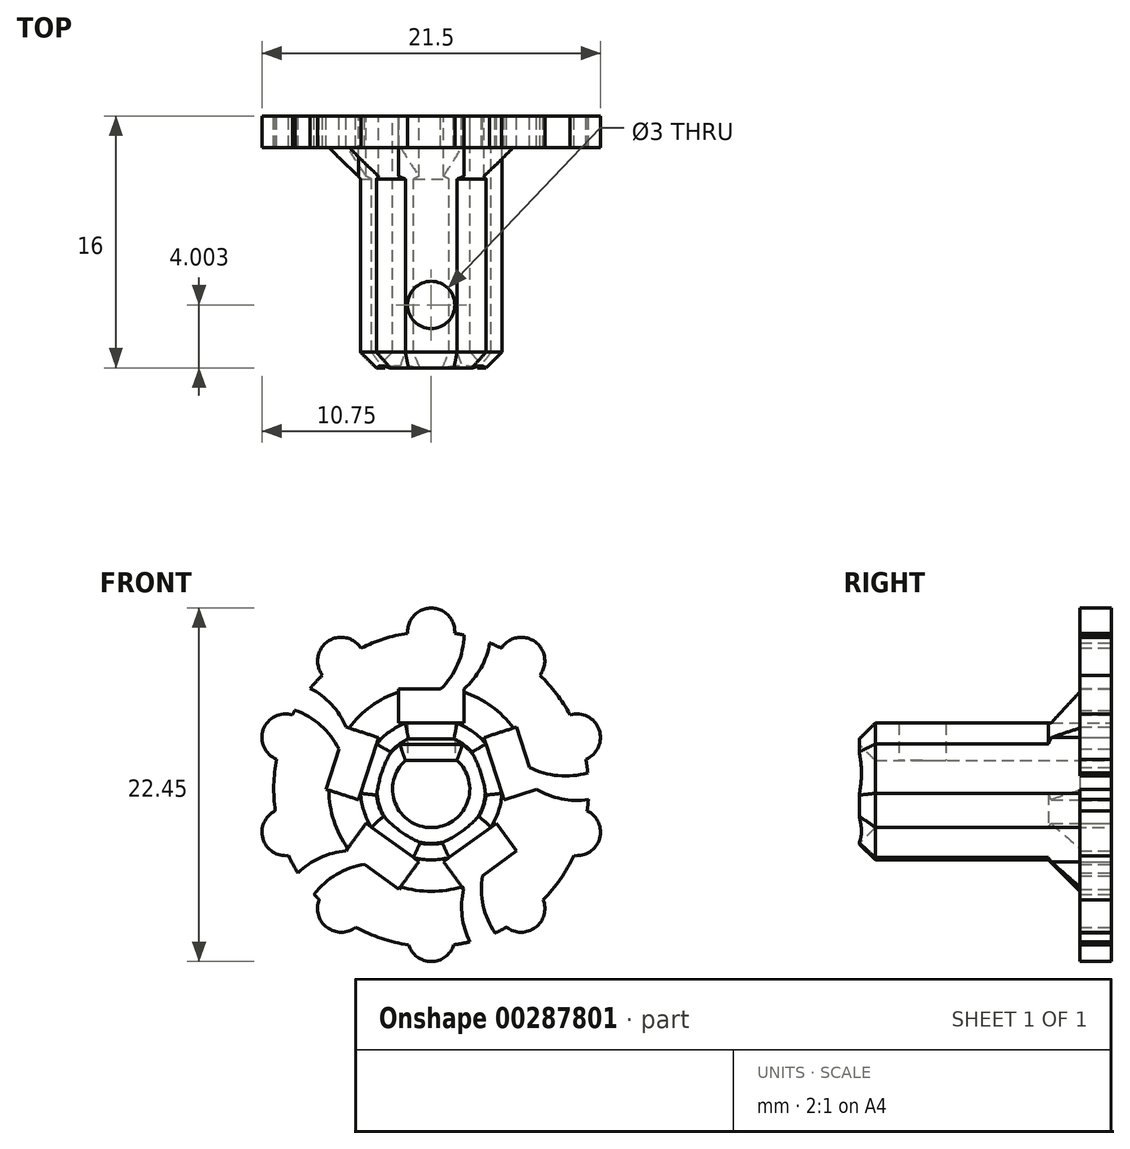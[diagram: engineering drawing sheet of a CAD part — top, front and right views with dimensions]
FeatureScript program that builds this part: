
annotation { "Feature Type Name" : "Feature", "Feature Type Description" : "" }
export const myFeature = defineFeature(function(context is Context, id is Id, definition is map)
    precondition{}
    {
        {
            var Q0;
            Q0=qCreatedBy(makeId("Front.planeOp"),FACE);
            var sketch = newSketch(context, id + "F0", { "sketchPlane" : qUnion([Q0])});
            skCircle(sketch, "E0", {"center": v(0, 0) * mm, "radius": 2.45 * mm});
            skLineSegment(sketch, "E1", {"start": v(-1.64, 1.82) * mm, "end": v(1.64, 1.82) * mm});
            skCircle(sketch, "E2", {"center": v(0, 0) * mm, "radius": 10 * mm});
            skArc(sketch, "E3", {"start": v(1.5, 9.89) * mm, "mid": v(0, 11.5) * mm, "end": v(-1.5, 9.89) * mm});
            skArc(sketch, "E4.1.0", {"start": v(-4.44, 8.93) * mm, "mid": v(-6.6, 9.36) * mm, "end": v(-6.86, 7.17) * mm});
            skArc(sketch, "E4.2.0", {"start": v(-8.68, 4.67) * mm, "mid": v(-10.68, 3.74) * mm, "end": v(-9.6, 1.82) * mm});
            skArc(sketch, "E4.3.0", {"start": v(-9.6, -1.27) * mm, "mid": v(-10.68, -3.2) * mm, "end": v(-8.68, -4.12) * mm});
            skArc(sketch, "E4.4.0", {"start": v(-6.86, -6.62) * mm, "mid": v(-6.6, -8.8) * mm, "end": v(-4.44, -8.38) * mm});
            skArc(sketch, "E4.5.0", {"start": v(-1.5, -9.34) * mm, "mid": v(0, -10.95) * mm, "end": v(1.5, -9.34) * mm});
            skArc(sketch, "E4.6.0", {"start": v(4.44, -8.38) * mm, "mid": v(6.6, -8.8) * mm, "end": v(6.86, -6.62) * mm});
            skArc(sketch, "E4.7.0", {"start": v(8.68, -4.12) * mm, "mid": v(10.68, -3.2) * mm, "end": v(9.6, -1.27) * mm});
            skArc(sketch, "E4.8.0", {"start": v(9.6, 1.82) * mm, "mid": v(10.68, 3.74) * mm, "end": v(8.68, 4.67) * mm});
            skArc(sketch, "E4.9.0", {"start": v(6.86, 7.17) * mm, "mid": v(6.6, 9.36) * mm, "end": v(4.44, 8.93) * mm});
            skPoint(sketch, "E4.center", {"position": v(0, 0.27) * mm});
            skPoint(sketch, "E5.1.0", {"position": v(0.35, -0.11) * mm});
            skLineSegment(sketch, "E6.bottom", {"start": v(2.08, 6.36) * mm, "end": v(-2.07, 6.36) * mm});
            skLineSegment(sketch, "E6.top", {"start": v(2.08, 4.2) * mm, "end": v(-2.07, 4.2) * mm});
            skLineSegment(sketch, "E6.left", {"start": v(2.08, 6.36) * mm, "end": v(2.08, 4.2) * mm});
            skLineSegment(sketch, "E6.right", {"start": v(-2.07, 6.36) * mm, "end": v(-2.07, 4.2) * mm});
            skPoint(sketch, "E6.middle", {"position": v(0, 5.27) * mm});
            skArc(sketch, "E7", {"start": v(0.6, 6.36) * mm, "mid": v(1.68, 7.93) * mm, "end": v(2.1, 9.78) * mm});
            skArc(sketch, "E8", {"start": v(2.08, 6.36) * mm, "mid": v(3.15, 7.68) * mm, "end": v(3.72, 9.28) * mm});
            skLineSegment(sketch, "E9.1.0", {"start": v(-3.34, 3.27) * mm, "end": v(-4.63, -0.68) * mm});
            skArc(sketch, "E9.1.1", {"start": v(-5.86, 2.54) * mm, "mid": v(-7.02, 4.05) * mm, "end": v(-8.65, 5) * mm});
            skLineSegment(sketch, "E9.1.2", {"start": v(-5.4, 3.94) * mm, "end": v(-6.69, 0) * mm});
            skLineSegment(sketch, "E9.1.3", {"start": v(-5.4, 3.94) * mm, "end": v(-3.34, 3.27) * mm});
            skPoint(sketch, "E9.1.4", {"position": v(-5.02, 1.63) * mm});
            skArc(sketch, "E9.1.5", {"start": v(-5.4, 3.94) * mm, "mid": v(-6.33, 5.37) * mm, "end": v(-7.68, 6.4) * mm});
            skLineSegment(sketch, "E9.1.6", {"start": v(-6.69, 0) * mm, "end": v(-4.63, -0.68) * mm});
            skLineSegment(sketch, "E9.2.0", {"start": v(-4.14, -2.17) * mm, "end": v(-0.78, -4.6) * mm});
            skArc(sketch, "E9.2.1", {"start": v(-4.23, -4.79) * mm, "mid": v(-6.02, -5.43) * mm, "end": v(-7.44, -6.68) * mm});
            skLineSegment(sketch, "E9.2.2", {"start": v(-5.42, -3.92) * mm, "end": v(-2.06, -6.36) * mm});
            skLineSegment(sketch, "E9.2.3", {"start": v(-5.42, -3.92) * mm, "end": v(-4.14, -2.17) * mm});
            skPoint(sketch, "E9.2.4", {"position": v(-3.1, -4.27) * mm});
            skArc(sketch, "E9.2.5", {"start": v(-5.42, -3.92) * mm, "mid": v(-7.06, -4.36) * mm, "end": v(-8.46, -5.33) * mm});
            skLineSegment(sketch, "E9.2.6", {"start": v(-2.06, -6.36) * mm, "end": v(-0.78, -4.6) * mm});
            skLineSegment(sketch, "E9.3.0", {"start": v(0.78, -4.6) * mm, "end": v(4.14, -2.17) * mm});
            skArc(sketch, "E9.3.1", {"start": v(3.25, -5.5) * mm, "mid": v(3.3, -7.4) * mm, "end": v(4.06, -9.14) * mm});
            skLineSegment(sketch, "E9.3.2", {"start": v(2.06, -6.36) * mm, "end": v(5.42, -3.92) * mm});
            skLineSegment(sketch, "E9.3.3", {"start": v(2.06, -6.36) * mm, "end": v(0.78, -4.6) * mm});
            skPoint(sketch, "E9.3.4", {"position": v(3.1, -4.27) * mm});
            skArc(sketch, "E9.3.5", {"start": v(2.06, -6.36) * mm, "mid": v(1.97, -8.06) * mm, "end": v(2.45, -9.7) * mm});
            skLineSegment(sketch, "E9.3.6", {"start": v(5.42, -3.92) * mm, "end": v(4.14, -2.17) * mm});
            skLineSegment(sketch, "E9.4.0", {"start": v(4.63, -0.68) * mm, "end": v(3.34, 3.27) * mm});
            skArc(sketch, "E9.4.1", {"start": v(6.23, 1.39) * mm, "mid": v(8.06, 0.85) * mm, "end": v(9.95, 1.03) * mm});
            skLineSegment(sketch, "E9.4.2", {"start": v(6.69, 0) * mm, "end": v(5.4, 3.94) * mm});
            skLineSegment(sketch, "E9.4.3", {"start": v(6.69, 0) * mm, "end": v(4.63, -0.68) * mm});
            skPoint(sketch, "E9.4.4", {"position": v(5.02, 1.63) * mm});
            skArc(sketch, "E9.4.5", {"start": v(6.69, 0) * mm, "mid": v(8.28, -0.62) * mm, "end": v(9.98, -0.67) * mm});
            skLineSegment(sketch, "E9.4.6", {"start": v(5.4, 3.94) * mm, "end": v(3.34, 3.27) * mm});
            skSolve(sketch);
        }
        {
            var Q0;
            Q0=makeQuery(id+"F0.imprint","IMPRINT",FACE,{"disambiguationData":[TD([[makeQuery(id+"F0.imprint","IMPRINT",EDGE,{"derivedFrom":sQuery(id+"F0.wireOp",EDGE,"E2")}),1.0]])]});
            var Q1;
            {var subQ0=sQuery(id+"F0.wireOp",EDGE,"E1");Q1=makeQuery(id+"F0.imprint","IMPRINT",FACE,{"disambiguationData":[TD([[makeQuery(id+"F0.imprint","IMPRINT",EDGE,{"derivedFrom":subQ0}),1.0]])]});}
            var Q2;
            {var subQ0=sQuery(id+"F0.wireOp",EDGE,"E3");Q2=makeQuery(id+"F0.imprint","IMPRINT",FACE,{"disambiguationData":[TD([[makeQuery(id+"F0.imprint","IMPRINT",EDGE,{"derivedFrom":subQ0}),1.0]])]});}
            var Q3;
            {var subQ0=sQuery(id+"F0.wireOp",EDGE,"E4.9.0");Q3=makeQuery(id+"F0.imprint","IMPRINT",FACE,{"disambiguationData":[TD([[makeQuery(id+"F0.imprint","IMPRINT",EDGE,{"derivedFrom":subQ0}),1.0]])]});}
            var Q4;
            {var subQ0=sQuery(id+"F0.wireOp",EDGE,"E4.8.0");Q4=makeQuery(id+"F0.imprint","IMPRINT",FACE,{"disambiguationData":[TD([[makeQuery(id+"F0.imprint","IMPRINT",EDGE,{"derivedFrom":subQ0}),1.0]])]});}
            var Q5;
            {var subQ0=sQuery(id+"F0.wireOp",EDGE,"E4.7.0");Q5=makeQuery(id+"F0.imprint","IMPRINT",FACE,{"disambiguationData":[TD([[makeQuery(id+"F0.imprint","IMPRINT",EDGE,{"derivedFrom":subQ0}),1.0]])]});}
            var Q6;
            {var subQ0=sQuery(id+"F0.wireOp",EDGE,"E4.6.0");Q6=makeQuery(id+"F0.imprint","IMPRINT",FACE,{"disambiguationData":[TD([[makeQuery(id+"F0.imprint","IMPRINT",EDGE,{"derivedFrom":subQ0}),1.0]])]});}
            var Q7;
            {var subQ0=sQuery(id+"F0.wireOp",EDGE,"E4.5.0");Q7=makeQuery(id+"F0.imprint","IMPRINT",FACE,{"disambiguationData":[TD([[makeQuery(id+"F0.imprint","IMPRINT",EDGE,{"derivedFrom":subQ0}),1.0]])]});}
            var Q8;
            {var subQ0=sQuery(id+"F0.wireOp",EDGE,"E4.4.0");Q8=makeQuery(id+"F0.imprint","IMPRINT",FACE,{"disambiguationData":[TD([[makeQuery(id+"F0.imprint","IMPRINT",EDGE,{"derivedFrom":subQ0}),1.0]])]});}
            var Q9;
            {var subQ0=sQuery(id+"F0.wireOp",EDGE,"E4.3.0");Q9=makeQuery(id+"F0.imprint","IMPRINT",FACE,{"disambiguationData":[TD([[makeQuery(id+"F0.imprint","IMPRINT",EDGE,{"derivedFrom":subQ0}),1.0]])]});}
            var Q10;
            {var subQ0=sQuery(id+"F0.wireOp",EDGE,"E4.2.0");Q10=makeQuery(id+"F0.imprint","IMPRINT",FACE,{"disambiguationData":[TD([[makeQuery(id+"F0.imprint","IMPRINT",EDGE,{"derivedFrom":subQ0}),1.0]])]});}
            var Q11;
            {var subQ0=sQuery(id+"F0.wireOp",EDGE,"E4.1.0");Q11=makeQuery(id+"F0.imprint","IMPRINT",FACE,{"disambiguationData":[TD([[makeQuery(id+"F0.imprint","IMPRINT",EDGE,{"derivedFrom":subQ0}),1.0]])]});}
            extrude(context, id + "F1", {"entities" : qUnion([Q0, Q1, Q2, Q3, Q4, Q5, Q6, Q7, Q8, Q9, Q10, Q11]), "depth" : 2 * mm});
        }
        {
            var Q0;
            Q0=makeQuery(id+"F1.opExtrude","CAP_FACE",FACE,{"disambiguationData":[OSD([sQuery(id+"F0.wireOp",EDGE,"E0"),sQuery(id+"F0.wireOp",EDGE,"E1"),sQuery(id+"F0.wireOp",EDGE,"E2")])],"isStart":false});
            var sketch = newSketch(context, id + "F2", { "sketchPlane" : qUnion([Q0])});
            skCircle(sketch, "E10", {"center": v(0, 0) * mm, "radius": 2.45 * mm});
            skCircle(sketch, "E11", {"center": v(0, 0) * mm, "radius": 4.5 * mm});
            skLineSegment(sketch, "E12", {"start": v(-1.64, 1.82) * mm, "end": v(1.64, 1.82) * mm});
            skSolve(sketch);
        }
        {
            var Q0;
            Q0=makeQuery(id+"F2.imprint","IMPRINT",FACE,{"disambiguationData":[TD([[makeQuery(id+"F2.imprint","IMPRINT",EDGE,{"derivedFrom":sQuery(id+"F2.wireOp",EDGE,"E11")}),1.0]])]});
            var Q1;
            {var subQ0=sQuery(id+"F2.wireOp",EDGE,"E12");Q1=makeQuery(id+"F2.imprint","IMPRINT",FACE,{"disambiguationData":[TD([[makeQuery(id+"F2.imprint","IMPRINT",EDGE,{"derivedFrom":subQ0}),1.0]])]});}
            extrude(context, id + "F3", {"entities" : qUnion([Q0, Q1]), "operationType" : NewBodyOperationType.ADD, "depth" : 14 * mm});
        }
        {
            var Q0;
            Q0=makeQuery(id+"F3.opExtrude","CAP_FACE",FACE,{"disambiguationData":[OSD([sQuery(id+"F2.wireOp",EDGE,"E10"),sQuery(id+"F2.wireOp",EDGE,"E11"),sQuery(id+"F2.wireOp",EDGE,"E12")])],"isStart":false});
            chamfer(context, id + "F4", {"entities" : qUnion([Q0]), "width" : 1 * mm, "tangentPropagation" : true});
        }
        {
            var Q0;
            Q0=qCreatedBy(makeId("Top.planeOp"),FACE);
            var sketch = newSketch(context, id + "F5", { "sketchPlane" : qUnion([Q0])});
            skCircle(sketch, "E13", {"center": v(0, -12) * mm, "radius": 1.5 * mm});
            skSolve(sketch);
        }
        {
            var Q0;
            Q0 = qSketchRegion(id + "F5", true);
            extrude(context, id + "F6", {"entities" : qUnion([Q0]), "operationType" : NewBodyOperationType.REMOVE, "endBound" : BoundingType.THROUGH_ALL, "depth" : 25 * mm, "offsetDistance" : 25 * mm});
        }
        {
            var Q0;
            {var subQ0=sQuery(id+"F2.wireOp",EDGE,"E11");Q0=makeQuery(id+"F3.opExtrude","CAP_EDGE",EDGE,{"disambiguationData":[OSD([subQ0]),TDD([makeQuery(id+"F2.imprint","IMPRINT",EDGE,{"disambiguationData":[TD([[makeQuery(id+"F2.imprint","INTERSECT",VERTEX,{"derivedFrom":[makeQuery(id+"F1.opExtrude","CAP_EDGE",EDGE,{"disambiguationData":[OSD([sQuery(id+"F0.wireOp",EDGE,"E5.1.4")])],"isStart":false}),subQ0]}),-1.0]])],"derivedFrom":subQ0})])],"isStart":true});}
            var Q1;
            {var subQ0=sQuery(id+"F2.wireOp",EDGE,"E11");Q1=makeQuery(id+"F3.opExtrude","CAP_EDGE",EDGE,{"disambiguationData":[OSD([subQ0]),TDD([makeQuery(id+"F2.imprint","IMPRINT",EDGE,{"disambiguationData":[TD([[makeQuery(id+"F2.imprint","INTERSECT",VERTEX,{"derivedFrom":[makeQuery(id+"F1.opExtrude","CAP_EDGE",EDGE,{"disambiguationData":[OSD([sQuery(id+"F0.wireOp",EDGE,"Yoly1lNo-tx7u-mn2p-w88S-Tv0ivk6sYndL")])],"isStart":false}),subQ0]}),-1.0]])],"derivedFrom":subQ0})])],"isStart":true});}
            var Q2;
            {var subQ0=sQuery(id+"F2.wireOp",EDGE,"E11");Q2=makeQuery(id+"F3.opExtrude","CAP_EDGE",EDGE,{"disambiguationData":[OSD([subQ0]),TDD([makeQuery(id+"F2.imprint","IMPRINT",EDGE,{"disambiguationData":[TD([[makeQuery(id+"F2.imprint","INTERSECT",VERTEX,{"derivedFrom":[makeQuery(id+"F1.opExtrude","CAP_EDGE",EDGE,{"disambiguationData":[OSD([sQuery(id+"F0.wireOp",EDGE,"43pJ61Si-pv4y-dq7J-sl7Z-adkjH1YZFIZD")])],"isStart":false}),subQ0]}),1.0]])],"derivedFrom":subQ0})])],"isStart":true});}
            var Q3;
            {var subQ0=sQuery(id+"F2.wireOp",EDGE,"E11");Q3=makeQuery(id+"F3.opExtrude","CAP_EDGE",EDGE,{"disambiguationData":[OSD([subQ0]),TDD([makeQuery(id+"F2.imprint","IMPRINT",EDGE,{"disambiguationData":[TD([[makeQuery(id+"F2.imprint","INTERSECT",VERTEX,{"derivedFrom":[makeQuery(id+"F1.opExtrude","CAP_EDGE",EDGE,{"disambiguationData":[OSD([sQuery(id+"F0.wireOp",EDGE,"E5.3.4")])],"isStart":false}),subQ0]}),-1.0]])],"derivedFrom":subQ0})])],"isStart":true});}
            var Q4;
            {var subQ0=sQuery(id+"F2.wireOp",EDGE,"E11");Q4=makeQuery(id+"F3.opExtrude","CAP_EDGE",EDGE,{"disambiguationData":[OSD([subQ0]),TDD([makeQuery(id+"F2.imprint","IMPRINT",EDGE,{"disambiguationData":[TD([[makeQuery(id+"F2.imprint","INTERSECT",VERTEX,{"derivedFrom":[makeQuery(id+"F1.opExtrude","CAP_EDGE",EDGE,{"disambiguationData":[OSD([sQuery(id+"F0.wireOp",EDGE,"E5.2.4")])],"isStart":false}),subQ0]}),-1.0]])],"derivedFrom":subQ0})])],"isStart":true});}
            chamfer(context, id + "F7", {"entities" : qUnion([Q0, Q1, Q2, Q3, Q4]), "width" : 2 * mm, "tangentPropagation" : true});
        }
    });
